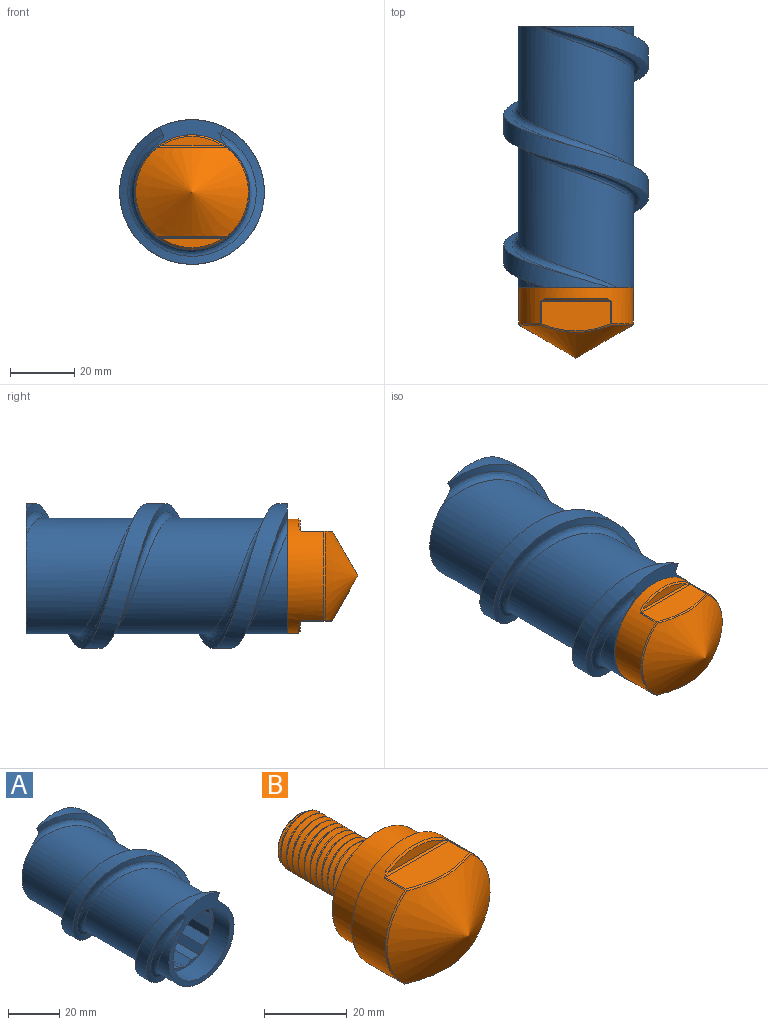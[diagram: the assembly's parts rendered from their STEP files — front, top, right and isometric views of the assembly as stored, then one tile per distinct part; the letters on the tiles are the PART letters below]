
ASSEMBLY  parts=2 mates=1
PART A: 34 faces, bbox 45x91.3x45 mm
  f0: cylinder r=22.5mm len=81.25mm, axis (0,1,0), area 1701.8mm2, adj f1,f2,f30,f31
  f1: plane 40.5x36mm, normal (0,-1,0), area 342.7mm2, adj f0,f27,f28,f29,f30,f31,f33
  f2: plane 40.5x36mm, normal (0,1,0), area 430.6mm2, adj f0,f3,f4,f5,f6,f7,f8,f9
  f3: plane 72.15x4.18mm, normal (0,0,-1), area 301.4mm2, adj f2,f4,f26,f32
  f4: plane 72.15x3.62mm, normal (-0.5,0,-0.87), area 301.4mm2, adj f2,f3,f5,f32
  f5: plane 72.15x3.62mm, normal (0.5,0,-0.87), area 301.4mm2, adj f2,f4,f6,f32
  f6: plane 72.15x4.18mm, normal (0,0,-1), area 301.4mm2, adj f2,f5,f7,f32
  f7: plane 72.15x3.62mm, normal (0.87,0,-0.5), area 301.4mm2, adj f2,f6,f8,f32
  f8: plane 72.15x3.62mm, normal (0.5,0,-0.87), area 301.4mm2, adj f2,f7,f9,f32
  f9: plane 72.15x4.18mm, normal (1,0,0), area 301.4mm2, adj f2,f8,f10,f32
  f10: plane 72.15x3.62mm, normal (0.87,0,-0.5), area 301.4mm2, adj f2,f9,f11,f32
  f11: plane 72.15x3.62mm, normal (0.87,0,0.5), area 301.4mm2, adj f2,f10,f12,f32
  f12: plane 72.15x4.18mm, normal (1,0,0), area 301.4mm2, adj f2,f11,f13,f32
  f13: plane 72.15x3.62mm, normal (0.5,0,0.87), area 301.4mm2, adj f2,f12,f14,f32
  f14: plane 72.15x3.62mm, normal (0.87,0,0.5), area 301.4mm2, adj f2,f13,f15,f32
  f15: plane 72.15x4.18mm, normal (0,0,1), area 301.4mm2, adj f2,f14,f16,f32
  f16: plane 72.15x3.62mm, normal (0.5,0,0.87), area 301.4mm2, adj f2,f15,f17,f32
  f17: plane 72.15x3.62mm, normal (-0.5,0,0.87), area 301.4mm2, adj f2,f16,f18,f32
  f18: plane 72.15x4.18mm, normal (0,0,1), area 301.4mm2, adj f2,f17,f19,f32
  f19: plane 72.15x3.62mm, normal (-0.87,0,0.5), area 301.4mm2, adj f2,f18,f20,f32
  f20: plane 72.15x3.62mm, normal (-0.5,0,0.87), area 301.4mm2, adj f2,f19,f21,f32
  f21: plane 72.15x4.18mm, normal (-1,0,0), area 301.4mm2, adj f2,f20,f22,f32
  f22: plane 72.15x3.62mm, normal (-0.87,0,0.5), area 301.4mm2, adj f2,f21,f23,f32
  f23: plane 72.15x3.62mm, normal (-0.87,0,-0.5), area 301.4mm2, adj f2,f22,f24,f32
  f24: plane 72.15x4.18mm, normal (-1,0,0), area 301.4mm2, adj f2,f23,f25,f32
  f25: plane 72.15x3.62mm, normal (-0.5,0,-0.87), area 301.4mm2, adj f2,f24,f26,f32
  f26: plane 72.15x3.62mm, normal (-0.87,0,-0.5), area 301.4mm2, adj f2,f3,f25,f32
  f27: bspline ~90.02x40mm, area 760.6mm2, adj f1,f2,f28,f30
  f28: cylinder r=18mm len=81.25mm, axis (0,-1,0), area 6934.4mm2, adj f1,f2,f27,f29
  f29: bspline ~90.02x40mm, area 760.4mm2, adj f1,f2,f28,f31
  f30: bspline ~84.64x45mm, area 697.8mm2, adj f0,f1,f2,f27
  f31: bspline ~84.64x45mm, area 697.8mm2, adj f0,f1,f2,f29
  f32: plane 31.2x31.2mm, normal (0,-1,0), area 87.9mm2, adj f3,f4,f5,f6,f7,f8,f9,f10
  f33: cylinder r=15.6mm len=31.2mm, axis (0,-1,0), area 892mm2, adj f1,f32
PART B: 39 faces, bbox 36.3x59.7x36.3 mm
  f0: plane 16.74x15.97mm, normal (0,-1,0), area 50.3mm2, adj f4,f5,f34,f36,f37
  f1: cylinder r=17.8mm len=35.6mm, axis (0,-1,0), area 900.7mm2, adj f8,f13,f15,f16,f17,f18,f22,f23
  f2: cone r=0mm half-angle=60deg, axis (0,1,0), area 1003.2mm2, adj f19,f22,f23,f24
  f3: plane 14.13x14.13mm, normal (0,1,0), area 151.9mm2, adj f33,f35,f37,f38
  f4: cylinder r=8mm len=22mm, axis (0,-1,0), area 12.4mm2, adj f0,f33,f34,f36,f38
  f5: cylinder r=6.5mm len=13mm, axis (0,-1,0), area 163.4mm2, adj f0,f6
  f6: plane 31x31mm, normal (0,1,0), area 622mm2, adj f5,f7
  f7: cylinder r=15.5mm len=31mm, axis (0,-1,0), area 876.5mm2, adj f6,f8
  f8: plane 35.6x35.6mm, normal (0,1,0), area 240.6mm2, adj f1,f7
  f9: plane 21.93x9.42mm, normal (0,0,-1), area 180.8mm2, adj f24,f27,f28,f29
  f10: plane 18.87x2.8mm, normal (0,-1,0), area 35.8mm2, adj f29,f32
  f11: plane 21.93x9.42mm, normal (0,0,1), area 180.8mm2, adj f14,f17,f18,f19
  f12: plane 18.87x2.8mm, normal (0,-1,0), area 35.8mm2, adj f13,f14
  f13: cone r=17.8mm half-angle=45deg, axis (0,1,0), area 14.3mm2, adj f1,f12,f15,f16
  f14: plane 21.64x0.5mm, normal (0,-0.71,0.71), area 14.3mm2, adj f11,f12,f15,f16
  f15: bspline ~1.73x1.08mm, area 0.7mm2, adj f1,f13,f14,f17
  f16: bspline ~1.7x1.03mm, area 0.7mm2, adj f1,f13,f14,f18
  f17: plane 6.93x0.31mm, normal (0.33,0,0.94), area 2.3mm2, adj f1,f11,f15,f20
  f18: plane 6.93x0.31mm, normal (-0.33,0,0.94), area 2.3mm2, adj f1,f11,f16,f21
  f19: bspline ~21.95x2.63mm, area 11.6mm2, adj f2,f11,f20,f21
  f20: plane 0.44x0.31mm, normal (0.29,-0.48,0.83), area 0.1mm2, adj f17,f19,f22
  f21: plane 0.43x0.31mm, normal (-0.29,-0.48,0.83), area 0.1mm2, adj f18,f19,f23
  f22: cone r=17.55mm half-angle=30deg, axis (0,1,0), area 15.8mm2, adj f1,f2,f20,f25
  f23: cone r=17.55mm half-angle=30deg, axis (0,1,0), area 15.8mm2, adj f1,f2,f21,f26
  f24: bspline ~21.95x2.63mm, area 11.6mm2, adj f2,f9,f25,f26
  f25: plane 0.43x0.31mm, normal (0.29,-0.48,-0.83), area 0.1mm2, adj f22,f24,f27
  f26: plane 0.43x0.31mm, normal (-0.29,-0.48,-0.83), area 0.1mm2, adj f23,f24,f28
  f27: plane 6.93x0.31mm, normal (0.33,0,-0.94), area 2.3mm2, adj f1,f9,f25,f30
  f28: plane 6.93x0.31mm, normal (-0.33,0,-0.94), area 2.3mm2, adj f1,f9,f26,f31
  f29: plane 21.64x0.5mm, normal (0,-0.71,-0.71), area 14.3mm2, adj f9,f10,f30,f31
  f30: bspline ~1.7x1.03mm, area 0.7mm2, adj f1,f27,f29,f32
  f31: bspline ~1.73x1.08mm, area 0.7mm2, adj f1,f28,f29,f32
  f32: cone r=17.8mm half-angle=45deg, axis (0,1,0), area 14.3mm2, adj f1,f10,f30,f31
  f33: cone r=8mm half-angle=45deg, axis (0,-1,0), area 27.2mm2, adj f3,f4,f35,f36,f38
  f34: plane 1.39x0.98mm, normal (0,0,1), area 0.8mm2, adj f0,f4,f37,f38
  f35: plane 1.39x1.02mm, normal (0,0,1), area 0.3mm2, adj f3,f33,f36,f37
  f36: bspline ~24.04x18.48mm, area 735.1mm2, adj f0,f4,f33,f35,f37
  f37: bspline ~23.83x15.64mm, area 290.1mm2, adj f0,f3,f34,f35,f36,f38
  f38: bspline ~23.71x18.48mm, area 724mm2, adj f3,f4,f33,f34,f37
PLACE A t=(-600,0,0)mm fixed
PLACE B t=(0,-81.25,0)mm
MATE fastened B.f1 <-> A.f0  axis (0,1,0) through (0,-81.25,0)mm
